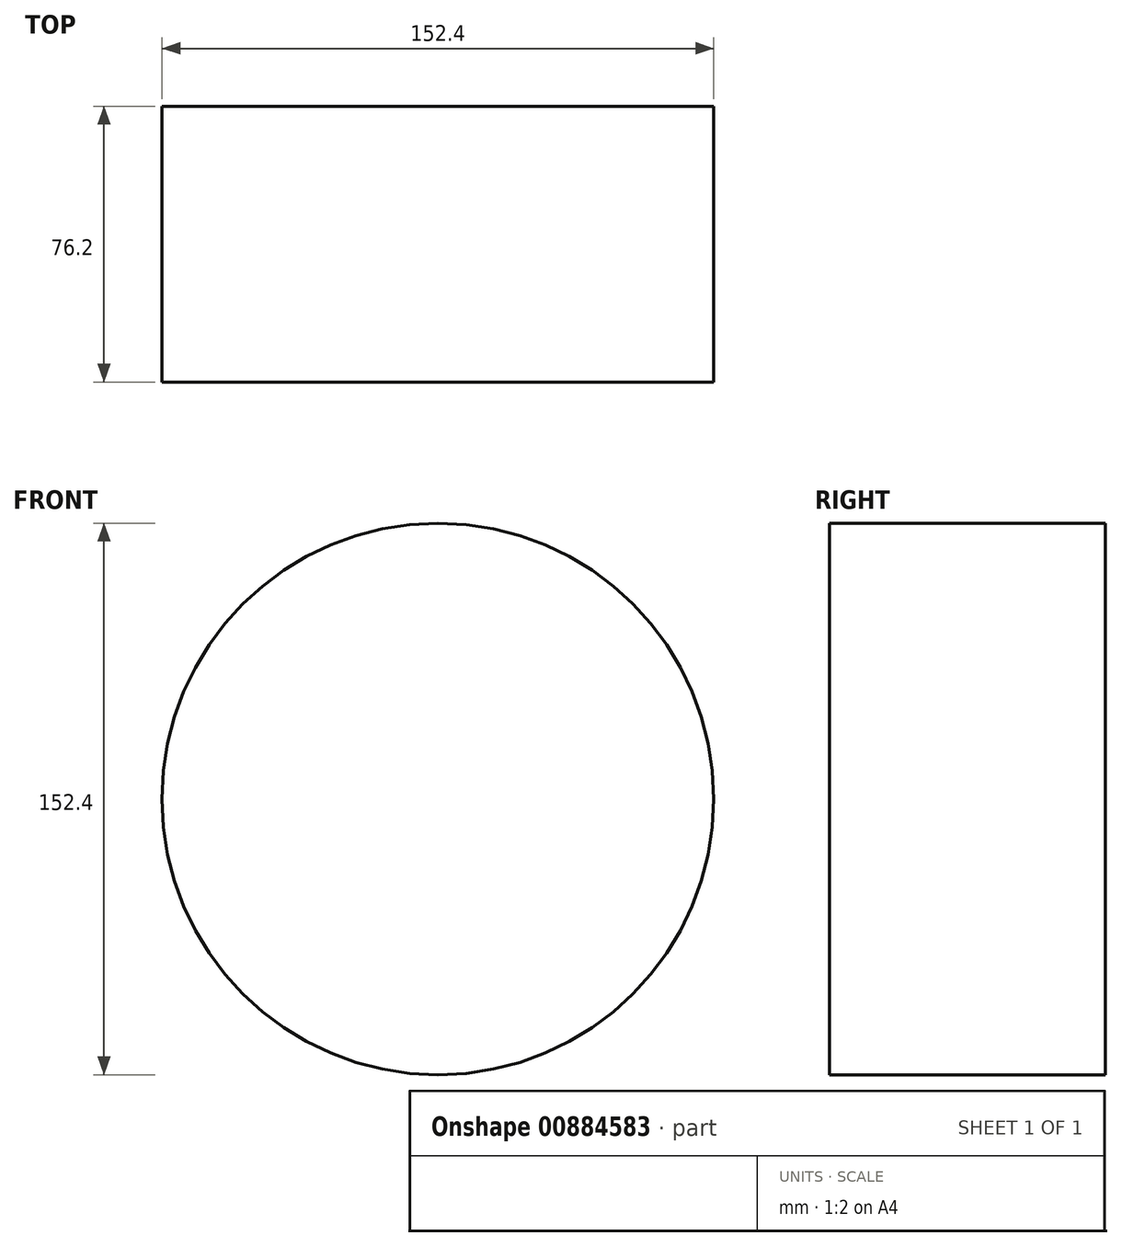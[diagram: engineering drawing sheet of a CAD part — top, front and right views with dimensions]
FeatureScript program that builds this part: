
annotation { "Feature Type Name" : "Feature", "Feature Type Description" : "" }
export const myFeature = defineFeature(function(context is Context, id is Id, definition is map)
    precondition{}
    {
        {
            var Q0;
            Q0=qCreatedBy(makeId("Front.planeOp"),FACE);
            var sketch = newSketch(context, id + "F0", { "sketchPlane" : qUnion([Q0])});
            skCircle(sketch, "E0", {"center": v(0, 0) * mm, "radius": 76.2 * mm});
            skSolve(sketch);
        }
        {
            var Q0;
            Q0=makeQuery(id+"F0.imprint","IMPRINT",FACE,{"disambiguationData":[TD([[makeQuery(id+"F0.imprint","IMPRINT",EDGE,{"derivedFrom":sQuery(id+"F0.wireOp",EDGE,"E0")}),1.0]])]});
            extrude(context, id + "F1", {"entities" : qUnion([Q0]), "depth" : 76.2 * mm, "offsetDistance" : 25.4 * mm});
        }
    });
